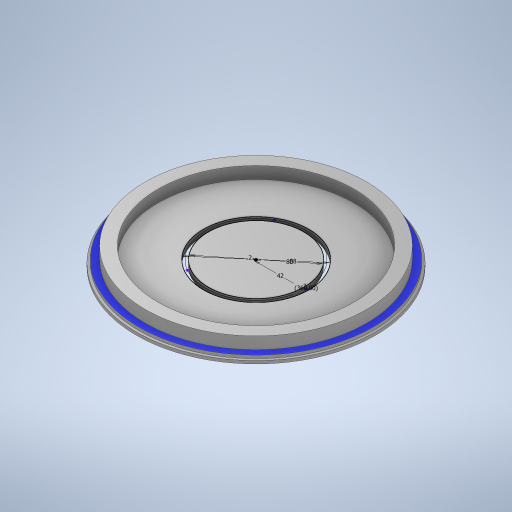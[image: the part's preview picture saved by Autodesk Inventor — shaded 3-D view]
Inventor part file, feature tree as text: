
AUTODESK INVENTOR PART (.ipt)
format: ipt  version: 2024 (Build 280153000, 153)  size: 441,344 bytes
history: native  units: mm
features: extrude x6, sketch x5, revolve x1
ambient origin geometry x8: Origin, YZ Plane, XZ Plane, XY Plane, X Axis, Y Axis, Z Axis, Center Point
bodies: Solid1 (feature_tree)
feature tree (12):
  extrude  "Extrusion1"  Depth=5.0mm TaperAngle=0.0deg
  sketch  "Sketch8"  dims[d17=2.0mm d18=2.0mm]
  extrude  "Extrusion4"  Depth=2.0mm
  revolve  "Revolution2"  Angle=360.0deg
  extrude  "Extrusion5"  Depth=185.0mm
  extrude  "Extrusion6"  Depth=10.0mm
  extrude  "Extrusion7"  Depth=10.0mm
  extrude  "Extrusion8"  TaperAngle=90.0deg  [1 undecoded]
  sketch  "Sketch1"  dims[d0=200.0mm d1=5.0mm d2=0.0mm]
  sketch  "Sketch9"  dims[d19=42.0mm d20=30.0mm d22=360.0deg]
  sketch  "Sketch10"  dims[d27=700.0mm d29=360.0deg d31=185.0mm]
  sketch  "Sketch11"  dims[d32=10.0mm d33=0.0mm d34=2.0mm d35=10.0mm d36=90.0deg d37=164.0mm d38=5.0mm d39=0.0mm d40=180.0mm d41=170.0mm d42=5.0mm d43=0.0mm d44=10.0mm d45=0.0mm d46=88.0mm d47=80.0mm d48=10.0mm d49=0.0mm]
note: 1 required parameter value undecoded (feature->parameter linkage not recoverable at this tier; creation-order binding heuristic only, values carry confidence <= 0.55)
